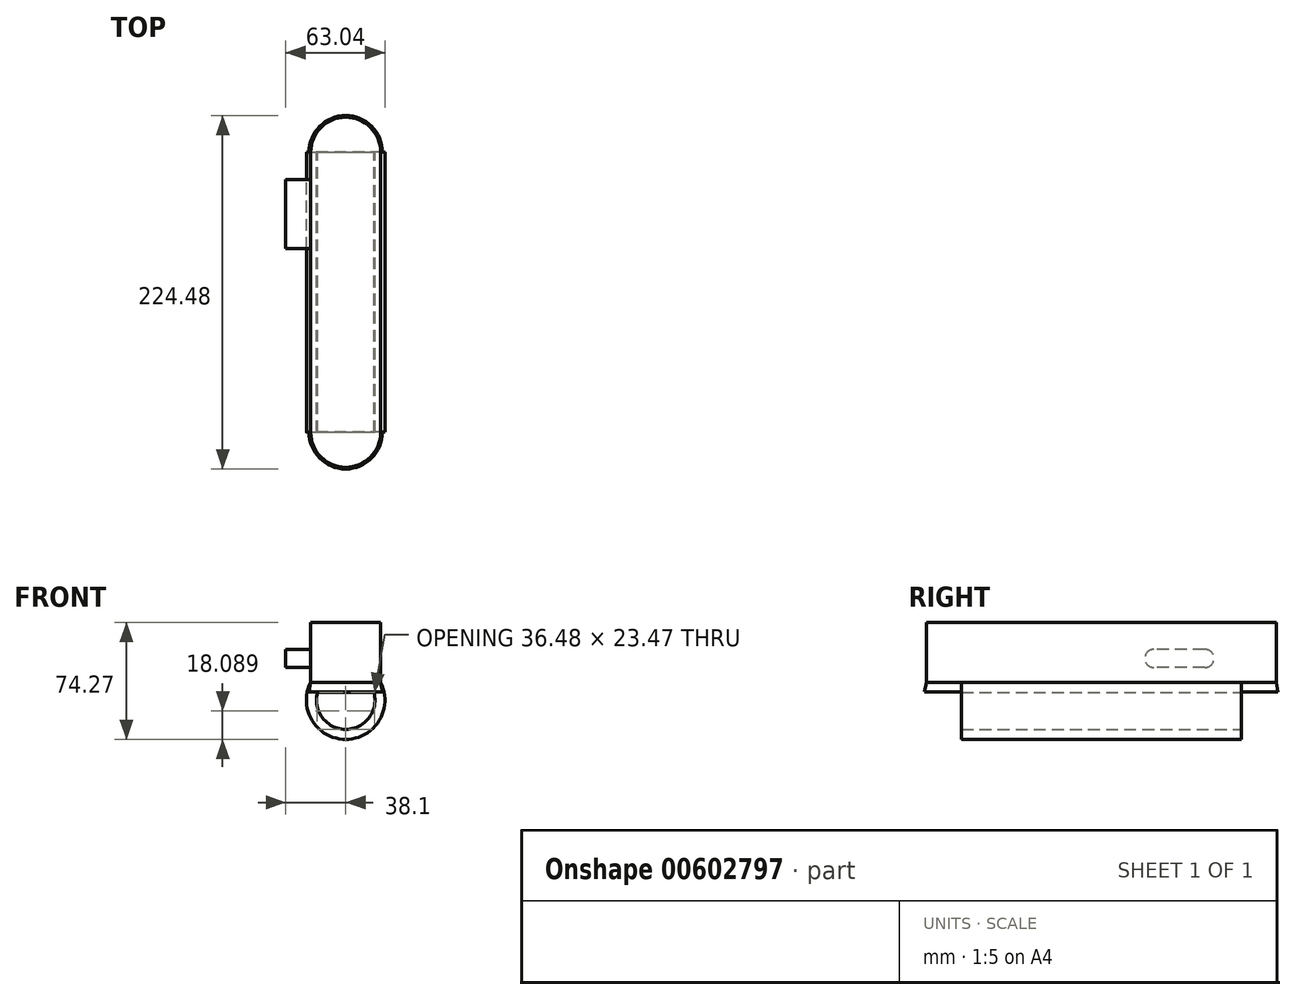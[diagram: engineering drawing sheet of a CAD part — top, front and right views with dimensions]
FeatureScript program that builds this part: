
annotation { "Feature Type Name" : "Feature", "Feature Type Description" : "" }
export const myFeature = defineFeature(function(context is Context, id is Id, definition is map)
    precondition{}
    {
        {
            var Q0;
            Q0=qCreatedBy(makeId("Front.planeOp"),FACE);
            var sketch = newSketch(context, id + "F0", { "sketchPlane" : qUnion([Q0])});
            skArc(sketch, "E0", {"start": v(-22.26, 11.23) * mm, "mid": v(0, -24.94) * mm, "end": v(22.26, 11.23) * mm});
            skLineSegment(sketch, "E1", {"start": v(-22.26, 11.23) * mm, "end": v(22.26, 11.23) * mm});
            skSolve(sketch);
        }
        {
            var Q0;
            Q0 = qSketchRegion(id + "F0", true);
            extrude(context, id + "F1", {"entities" : qUnion([Q0]), "depth" : 88.9 * mm, "offsetDistance" : 25.4 * mm, "hasSecondDirection" : true, "secondDirectionOppositeDirection" : true, "secondDirectionDepth" : 88.9 * mm});
        }
        {
            var Q0;
            Q0=makeQuery(id+"F1.opExtrude","CAP_FACE",FACE,{"disambiguationData":[OSD([sQuery(id+"F0.wireOp",EDGE,"E0")])],"isStart":false});
            var Q1;
            Q1=makeQuery(id+"F1.opExtrude","CAP_FACE",FACE,{"disambiguationData":[OSD([sQuery(id+"F0.wireOp",EDGE,"E0")])],"isStart":true});
            shell(context, id + "F2", {"entities" : qUnion([Q0, Q1]), "thickness" : 6.35 * mm});
        }
        {
            var Q0;
            Q0=makeQuery(id+"F1.opExtrude","SWEPT_FACE",FACE,{"disambiguationData":[OSD([sQuery(id+"F0.wireOp",EDGE,"E1")])]});
            var sketch = newSketch(context, id + "F3", { "sketchPlane" : qUnion([Q0])});
            skLineSegment(sketch, "E2.bottom", {"start": v(-22.26, 88.9) * mm, "end": v(22.26, 88.9) * mm});
            skLineSegment(sketch, "E2.top", {"start": v(-22.26, -88.9) * mm, "end": v(22.26, -88.9) * mm});
            skLineSegment(sketch, "E2.left", {"start": v(-22.26, 88.9) * mm, "end": v(-22.26, -88.9) * mm});
            skLineSegment(sketch, "E2.right", {"start": v(22.26, 88.9) * mm, "end": v(22.26, -88.9) * mm});
            skArc(sketch, "E3", {"start": v(-22.26, -88.9) * mm, "mid": v(0, -111.16) * mm, "end": v(22.26, -88.9) * mm});
            skArc(sketch, "E4", {"start": v(22.26, 88.9) * mm, "mid": v(0, 111.16) * mm, "end": v(-22.26, 88.9) * mm});
            skSolve(sketch);
        }
        {
            var Q0;
            Q0=makeQuery(id+"F3.imprint","IMPRINT",FACE,{"disambiguationData":[TD([[makeQuery(id+"F3.imprint","IMPRINT",EDGE,{"derivedFrom":sQuery(id+"F3.wireOp",EDGE,"E2.bottom")}),-1.0]])]});
            extrude(context, id + "F4", {"entities" : qUnion([Q0]), "operationType" : NewBodyOperationType.ADD, "depth" : 38.1 * mm, "offsetDistance" : 25.4 * mm});
        }
        {
            var Q0;
            Q0=makeQuery(id+"F3.imprint","IMPRINT",FACE,{"disambiguationData":[TD([[makeQuery(id+"F3.imprint","IMPRINT",EDGE,{"derivedFrom":sQuery(id+"F3.wireOp",EDGE,"E2.top")}),-1.0]])]});
            var Q1;
            Q1=makeQuery(id+"F3.imprint","IMPRINT",FACE,{"disambiguationData":[TD([[makeQuery(id+"F3.imprint","IMPRINT",EDGE,{"derivedFrom":sQuery(id+"F3.wireOp",EDGE,"E2.bottom")}),1.0]])]});
            extrude(context, id + "F5", {"entities" : qUnion([Q0, Q1]), "operationType" : NewBodyOperationType.ADD, "depth" : 38.1 * mm, "offsetDistance" : 25.4 * mm, "hasSecondDirection" : true, "secondDirectionOppositeDirection" : true, "secondDirectionDepth" : 6.1 * mm, "hasSecondDirectionDraft" : true, "secondDirectionDraftAngle" : 10 * degree});
        }
        {
            var Q0;
            Q0=makeQuery(id+"F4.opExtrude","SWEPT_FACE",FACE,{"disambiguationData":[OSD([sQuery(id+"F3.wireOp",EDGE,"E2.left")])]});
            var sketch = newSketch(context, id + "F6", { "sketchPlane" : qUnion([Q0])});
            skLineSegment(sketch, "E5.bottom", {"start": v(-65.75, 32.26) * mm, "end": v(-33.37, 32.26) * mm});
            skLineSegment(sketch, "E5.top", {"start": v(-65.75, 20.71) * mm, "end": v(-33.37, 20.71) * mm});
            skLineSegment(sketch, "E5.left", {"start": v(-65.75, 32.26) * mm, "end": v(-65.75, 20.71) * mm});
            skLineSegment(sketch, "E5.right", {"start": v(-33.37, 32.26) * mm, "end": v(-33.37, 20.71) * mm});
            skArc(sketch, "E6", {"start": v(-33.37, 32.26) * mm, "mid": v(-27.6, 26.49) * mm, "end": v(-33.37, 20.71) * mm});
            skArc(sketch, "E7", {"start": v(-65.75, 32.26) * mm, "mid": v(-71.53, 26.49) * mm, "end": v(-65.75, 20.71) * mm});
            skSolve(sketch);
        }
        {
            var Q0;
            Q0 = qSketchRegion(id + "F6", true);
            extrude(context, id + "F7", {"entities" : qUnion([Q0]), "operationType" : NewBodyOperationType.REMOVE, "oppositeDirection" : true, "depth" : 22.26 * mm, "offsetDistance" : 25.4 * mm});
        }
        {
            var Q0;
            Q0=makeQuery(id+"F7.boolean.opBoolean","COPY",FACE,{"derivedFrom":makeQuery(id+"F7.opExtrude","CAP_FACE",FACE,{"disambiguationData":[OSD([sQuery(id+"F6.wireOp",EDGE,"E5.bottom"),sQuery(id+"F6.wireOp",EDGE,"E5.top"),sQuery(id+"F6.wireOp",EDGE,"E6"),sQuery(id+"F6.wireOp",EDGE,"E7")])],"isStart":false})});
            var sketch = newSketch(context, id + "F8", { "sketchPlane" : qUnion([Q0])});
            skLineSegment(sketch, "E8.bottom", {"start": v(-65.75, 32.26) * mm, "end": v(-33.37, 32.26) * mm});
            skLineSegment(sketch, "E8.top", {"start": v(-65.75, 20.71) * mm, "end": v(-33.37, 20.71) * mm});
            skLineSegment(sketch, "E8.left", {"start": v(-65.75, 32.26) * mm, "end": v(-65.75, 20.71) * mm});
            skLineSegment(sketch, "E8.right", {"start": v(-33.37, 32.26) * mm, "end": v(-33.37, 20.71) * mm});
            skArc(sketch, "E9", {"start": v(-33.37, 32.26) * mm, "mid": v(-27.6, 26.49) * mm, "end": v(-33.37, 20.71) * mm});
            skArc(sketch, "E10", {"start": v(-65.75, 32.26) * mm, "mid": v(-71.53, 26.49) * mm, "end": v(-65.75, 20.71) * mm});
            skSolve(sketch);
        }
        {
            var Q0;
            Q0 = qSketchRegion(id + "F8", true);
            extrude(context, id + "F9", {"entities" : qUnion([Q0]), "operationType" : NewBodyOperationType.ADD, "depth" : 38.1 * mm, "offsetDistance" : 25.4 * mm});
        }
    });
